# Revit family: 6248 01_Anschlussbogen 90°
name_source: partatom
category: Rohrformteile
units: mm (PartAtom-declared; Revit-internal decimal feet)

## family parameters
Arbeitsebenenbasiert = Nein
Beim Laden mit Abzugskörper schneiden = Nein
Bemaßung runder Anschluss = Radius verwenden
Gemeinsam genutzt = Nein
Immer vertikal = Ja
OmniClass-Nummer = 23.60.30.11.14
OmniClass-Titel = Pipework Fittings
Teiletyp = Bogen

## types (1)
- G3/4 x G3/4
    Anschlussbogen = Messing CC770S, vernickelt
    Ausführung = Anschlussbogen 90° aus Messing, vernickelt, Rohranschluss mit Aussengewinde, freidrehende Überwurfmutter, konisch dichtend.
    Hersteller = HERZ Armaturen Ges.m.b.H.
    Hinweiß = Der O-Ring dient als zusätzliche Dichtung, bei Verlust ist der Anschlussbogen metallisch dichtend.
    K-Koeffizient-Tabelle = Regular 45, 90 and 180 Elbow
    Max. Betriebsdruck = 1000000.0 Pa
    Max. Betriebstemperatur = 110 °C
    Medium = Heizungswasser nach ÖNORM H5195 oder VDI- Richtlinie 2035.
Die Verwendung von Ethylen- oder Propyleneglykol in einem Mischungsverhältnis 25- 50% ist zulässig.
    Mutter = Messing CW614N, vernickelt
    O-Ring = EPDM
    SCRNCODE = 07;08;02
    SCRNSEQ = AWI;AWI_TYP="1001";2
    URL = www.herz-armaturen.at
    Verlustberechnungsmethode = K-Koeffizient aus Tabelle
    Vorgabe-Ansicht = 0 mm  [stored 0 ft]

note: [stored X ft] marks values corroborated as IEEE doubles in the binary element streams (Revit-internal decimal feet)
